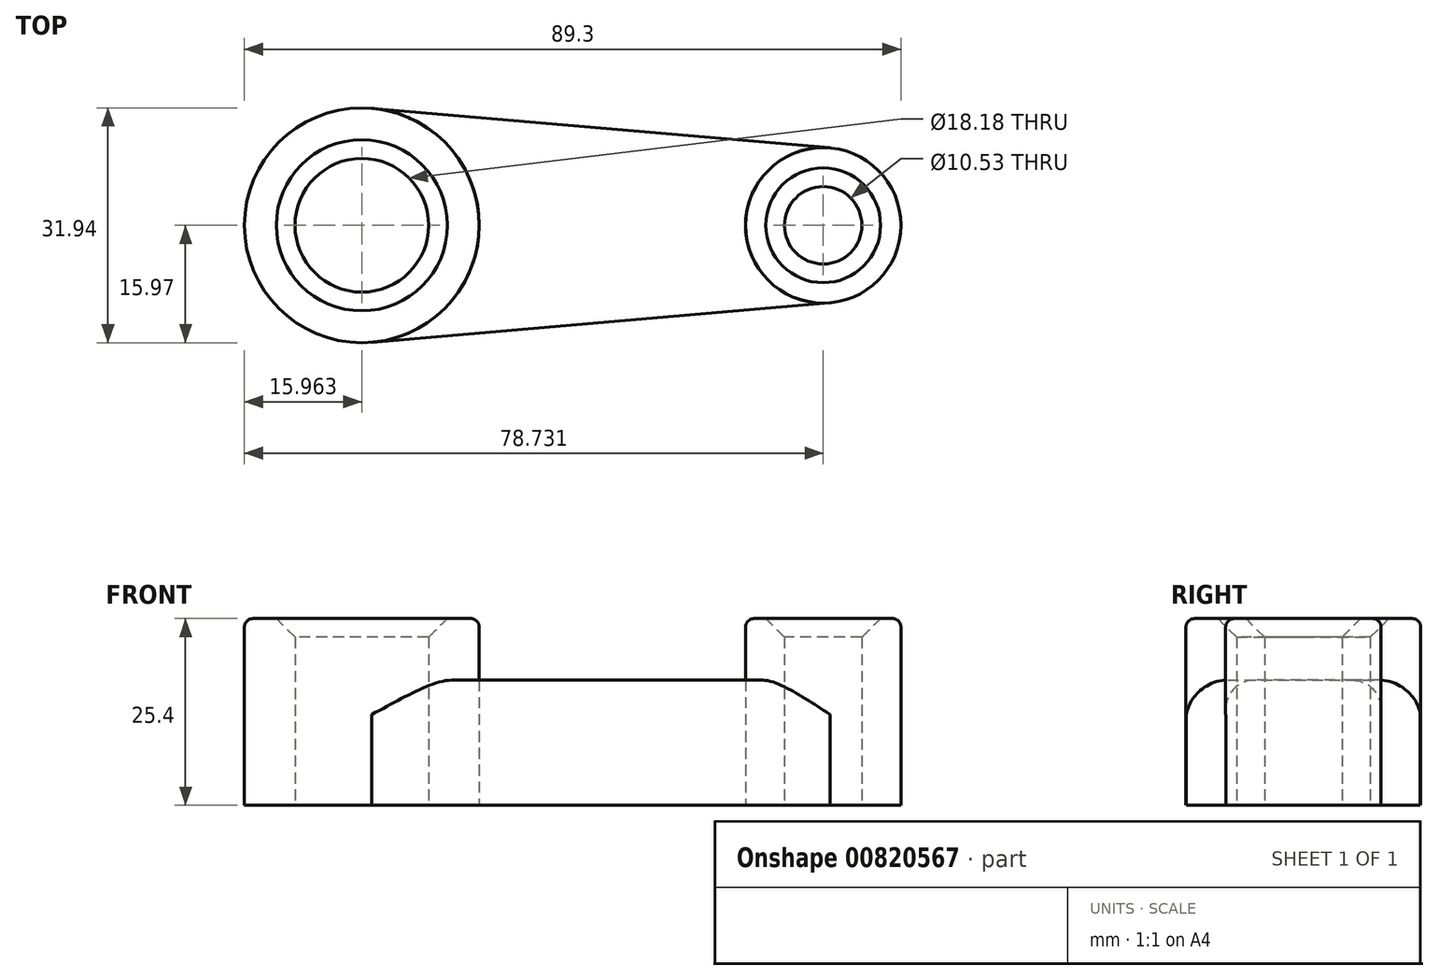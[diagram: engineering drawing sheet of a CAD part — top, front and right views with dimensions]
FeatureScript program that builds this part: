
annotation { "Feature Type Name" : "Feature", "Feature Type Description" : "" }
export const myFeature = defineFeature(function(context is Context, id is Id, definition is map)
    precondition{}
    {
        {
            var Q0;
            Q0=qCreatedBy(makeId("Top.planeOp"),FACE);
            var sketch = newSketch(context, id + "F0", { "sketchPlane" : qUnion([Q0])});
            skCircle(sketch, "E0", {"center": v(-31.25, 0) * mm, "radius": 15.97 * mm});
            skCircle(sketch, "E1", {"center": v(31.52, 0) * mm, "radius": 10.57 * mm});
            skLineSegment(sketch, "E2", {"start": v(-29.87, 15.9) * mm, "end": v(32.43, 10.53) * mm});
            skLineSegment(sketch, "E3", {"start": v(-29.87, -15.9) * mm, "end": v(32.43, -10.53) * mm});
            skCircle(sketch, "E4", {"center": v(-31.25, 0) * mm, "radius": 9.1 * mm});
            skCircle(sketch, "E5", {"center": v(31.52, 0) * mm, "radius": 5.26 * mm});
            skSolve(sketch);
        }
        {
            var Q0;
            Q0=makeQuery(id+"F0.imprint","IMPRINT",FACE,{"disambiguationData":[TD([[makeQuery(id+"F0.imprint","IMPRINT",EDGE,{"derivedFrom":sQuery(id+"F0.wireOp",EDGE,"E4")}),-1.0]])]});
            var Q1;
            Q1=makeQuery(id+"F0.imprint","IMPRINT",FACE,{"disambiguationData":[TD([[makeQuery(id+"F0.imprint","IMPRINT",EDGE,{"derivedFrom":sQuery(id+"F0.wireOp",EDGE,"E5")}),-1.0]])]});
            extrude(context, id + "F1", {"entities" : qUnion([Q0, Q1]), "depth" : 25.4 * mm, "offsetDistance" : 25.4 * mm});
        }
        {
            var Q0;
            {var subQ0=sQuery(id+"F0.wireOp",EDGE,"E2");Q0=makeQuery(id+"F0.imprint","IMPRINT",FACE,{"disambiguationData":[TD([[makeQuery(id+"F0.imprint","IMPRINT",EDGE,{"derivedFrom":subQ0}),-1.0]])]});}
            extrude(context, id + "F2", {"entities" : qUnion([Q0]), "depth" : 17.02 * mm, "offsetDistance" : 25.4 * mm});
        }
        {
            var Q0;
            Q0=makeQuery(id+"F1.opExtrude","CAP_EDGE",EDGE,{"disambiguationData":[OSD([sQuery(id+"F0.wireOp",EDGE,"E0")])],"isStart":false});
            var Q1;
            Q1=makeQuery(id+"F1.opExtrude","CAP_EDGE",EDGE,{"disambiguationData":[OSD([sQuery(id+"F0.wireOp",EDGE,"E1")])],"isStart":false});
            fillet(context, id + "F3", {"entities" : qUnion([Q0, Q1]), "radius" : 1.17 * mm, "tangentPropagation" : true, "allowEdgeOverflow" : false});
        }
        {
            var Q0;
            Q0=makeQuery(id+"F2.opExtrude","CAP_EDGE",EDGE,{"disambiguationData":[OSD([sQuery(id+"F0.wireOp",EDGE,"E3")])],"isStart":false});
            var Q1;
            Q1=makeQuery(id+"F2.opExtrude","CAP_EDGE",EDGE,{"disambiguationData":[OSD([sQuery(id+"F0.wireOp",EDGE,"E2")])],"isStart":false});
            fillet(context, id + "F4", {"entities" : qUnion([Q0, Q1]), "radius" : 4.66 * mm, "tangentPropagation" : true, "allowEdgeOverflow" : false});
        }
        {
            var Q0;
            Q0=makeQuery(id+"F1.opExtrude","CAP_EDGE",EDGE,{"disambiguationData":[OSD([sQuery(id+"F0.wireOp",EDGE,"E4")])],"isStart":false});
            var Q1;
            Q1=makeQuery(id+"F1.opExtrude","CAP_EDGE",EDGE,{"disambiguationData":[OSD([sQuery(id+"F0.wireOp",EDGE,"E5")])],"isStart":false});
            chamfer(context, id + "F5", {"entities" : qUnion([Q0, Q1]), "width" : 2.54 * mm, "tangentPropagation" : true});
        }
    });
